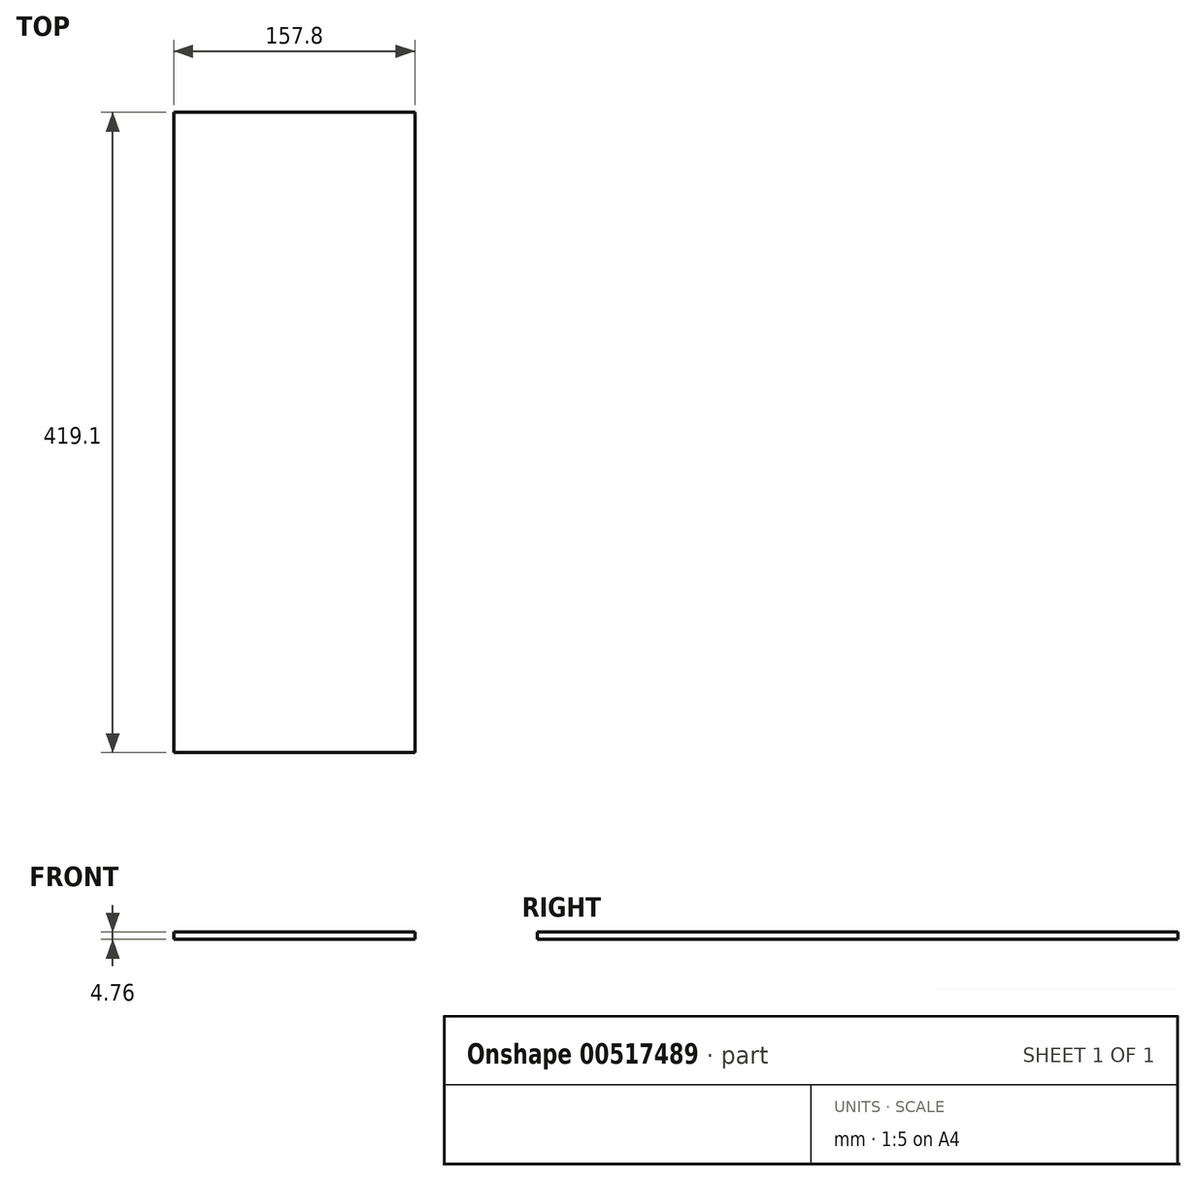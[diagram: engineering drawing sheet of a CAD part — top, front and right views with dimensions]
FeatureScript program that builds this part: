
annotation { "Feature Type Name" : "Feature", "Feature Type Description" : "" }
export const myFeature = defineFeature(function(context is Context, id is Id, definition is map)
    precondition{}
    {
        {
            var Q0;
            Q0=qCreatedBy(makeId("Top.planeOp"),FACE);
            var sketch = newSketch(context, id + "F0", { "sketchPlane" : qUnion([Q0])});
            skLineSegment(sketch, "E0.bottom", {"start": v(78.9, -209.55) * mm, "end": v(-78.9, -209.55) * mm});
            skLineSegment(sketch, "E0.top", {"start": v(78.9, 209.55) * mm, "end": v(-78.9, 209.55) * mm});
            skLineSegment(sketch, "E0.left", {"start": v(78.9, -209.55) * mm, "end": v(78.9, 209.55) * mm});
            skLineSegment(sketch, "E0.right", {"start": v(-78.9, -209.55) * mm, "end": v(-78.9, 209.55) * mm});
            skPoint(sketch, "E0.middle", {"position": v(0, 0) * mm});
            skSolve(sketch);
        }
        {
            var Q0;
            Q0=makeQuery(id+"F0.imprint","IMPRINT",FACE,{"disambiguationData":[TD([[makeQuery(id+"F0.imprint","IMPRINT",EDGE,{"derivedFrom":sQuery(id+"F0.wireOp",EDGE,"E0.bottom")}),-1.0]])]});
            extrude(context, id + "F1", {"entities" : qUnion([Q0]), "depth" : 4.76 * mm, "offsetDistance" : 25.4 * mm});
        }
    });
